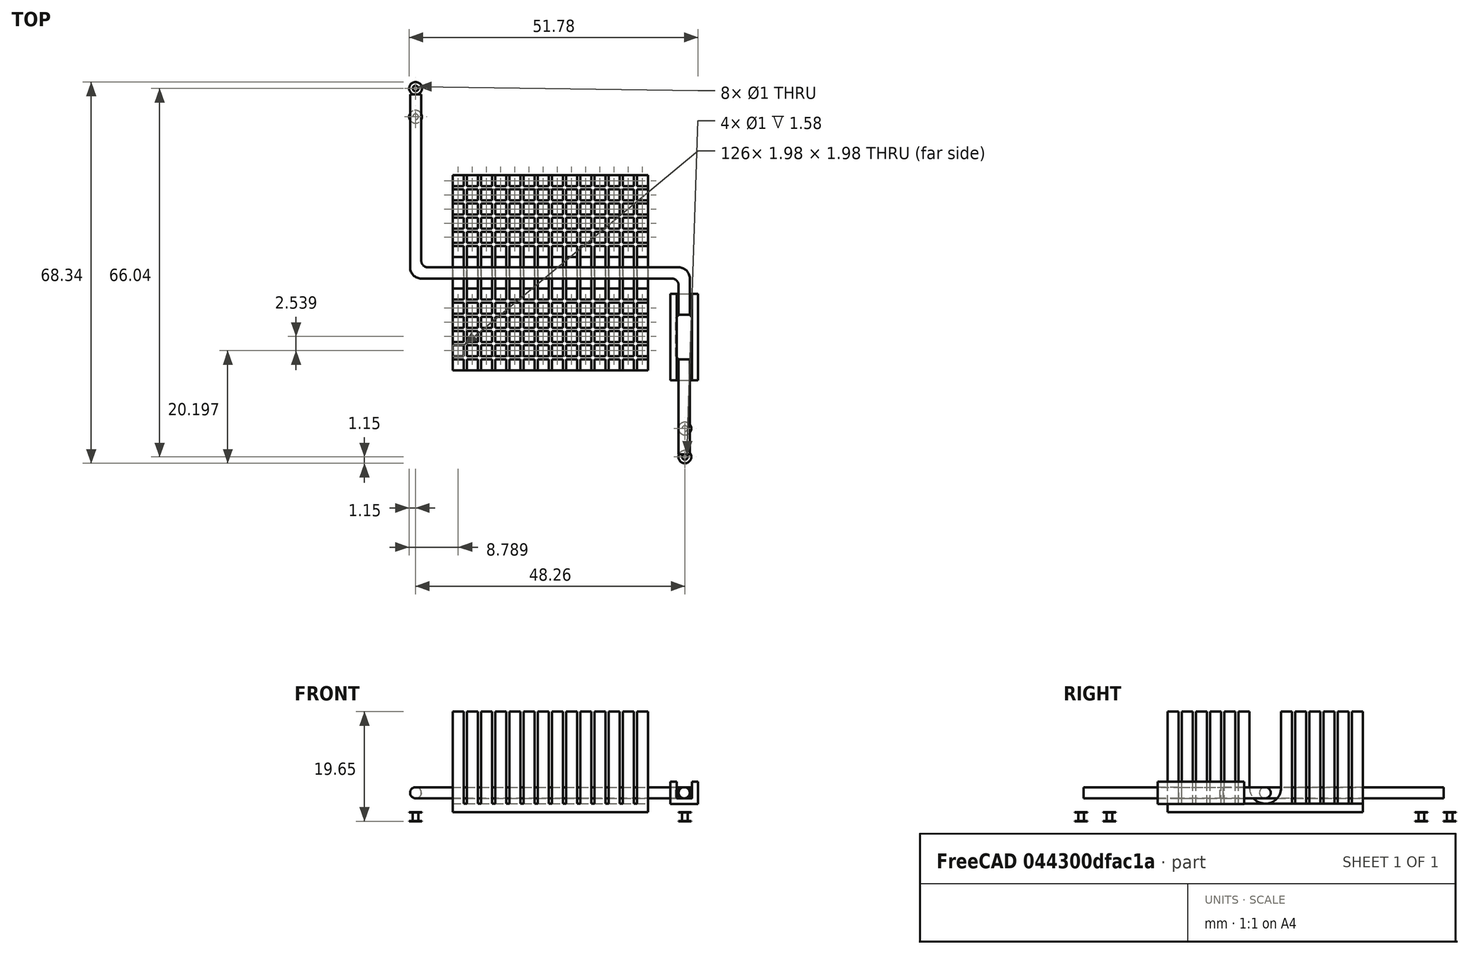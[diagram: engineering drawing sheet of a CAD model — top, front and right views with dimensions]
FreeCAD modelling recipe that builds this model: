
FCSTD DOCUMENT  (FreeCAD 0.20R29177 (Git))
Label: Aavid-heatsink2
License: All rights reserved
LicenseURL: http://en.wikipedia.org/wiki/All_rights_reserved
objects: PartDesign::AdditiveBox×7, PartDesign::Fillet×4, PartDesign::Body×4, Part::FeaturePython×3, Part::Feature×2, Sketcher::SketchObject×2, PartDesign::Chamfer×2, App::DocumentObjectGroup×1, PartDesign::SubtractiveBox×1, Part::Part2DObjectPython×1, PartDesign::Pad×1, App::Part×1
note: 41 computed .brp shape members not serialized (recipe doc carries the construction recipe); baked Part::Feature solids carry a one-line shape summary decoded from their .brp

FEATURE [Part::FeaturePython] FFab_lines  label="FFab"  # a2plus imported part (geometry in sourceFile) (typed FeaturePython)
  fixedPosition = true
FEATURE [Part::FeaturePython] THPs  label="PTHs"  # a2plus imported part (geometry in sourceFile) (typed FeaturePython)
  fixedPosition = true
FEATURE [Part::Feature] Shape001003  label="TopPads"
  shape: bbox 50.56 x 68.34 x 0.01 mm, 16 faces, 4 solids (baked)
FEATURE [Part::Feature] Shape001004  label="BotPads"
  shape: bbox 50.56 x 68.34 x 0.01 mm, 16 faces, 4 solids (baked)
FEATURE [App::DocumentObjectGroup] Heatsink_35x35mm_SpringFixation_fp
  Group = -> [FFab_lines,Shape001003,Shape001004,THPs]
FEATURE [Sketcher::SketchObject] Sketch  label="Pads_Poly"
  FullyConstrained = false
  MapMode = 5
  Support = -> [XY_Plane]
  sketch-geometry (56):
    g0: LineSegment StartX=-17.5 StartY=-17.45 StartZ=0 EndX=-17.5 EndY=17.55 EndZ=0
    g1: LineSegment StartX=-17.5 StartY=17.55 StartZ=0 EndX=-17.5 EndY=-17.55 EndZ=0
    g2: LineSegment StartX=-17.5 StartY=17.55 StartZ=0 EndX=17.55 EndY=17.5 EndZ=0
    g3: LineSegment StartX=17.55 StartY=17.5 StartZ=0 EndX=-17.5 EndY=17.45 EndZ=0
    g4: LineSegment StartX=17.55 StartY=17.5 StartZ=0 EndX=17.55 EndY=-17.5 EndZ=0
    g5: LineSegment StartX=17.5 StartY=-17.55 StartZ=0 EndX=17.45 EndY=17.5 EndZ=0
    g6: LineSegment StartX=17.5 StartY=-17.55 StartZ=0 EndX=-17.5 EndY=-17.55 EndZ=0
    g7: LineSegment StartX=-17.5 StartY=-17.45 StartZ=0 EndX=17.55 EndY=-17.5 EndZ=0
    g8: LineSegment StartX=-26.72 StartY=25.4 StartZ=0 EndX=-26.67 EndY=35.61 EndZ=0
    g9: LineSegment StartX=-26.67 StartY=35.61 StartZ=0 EndX=-26.62 EndY=25.4 EndZ=0
    g10: LineSegment StartX=-21.54 StartY=35.56 StartZ=0 EndX=-21.54 EndY=25.4 EndZ=0
    g11: LineSegment StartX=-21.64 StartY=25.4 StartZ=0 EndX=-21.64 EndY=35.56 EndZ=0
    g12: LineSegment StartX=-21.54 StartY=25.4 StartZ=0 EndX=-26.72 EndY=25.4 EndZ=0
    g13: LineSegment StartX=-26.72 StartY=25.4 StartZ=0 EndX=-21.54 EndY=25.4 EndZ=0
    g14: LineSegment StartX=-22.81 StartY=25.4 StartZ=0 EndX=-22.8271 EndY=2.54 EndZ=0
    g15: ArcOfCircle CenterX=-21.59 CenterY=2.55711 CenterZ=0 NormalX=0 NormalY=0 NormalZ=1 AngleXU=-1.5708 Radius=1.23726 StartAngle=4.72622 EndAngle=6.28319
    g16: LineSegment StartX=-21.59 StartY=1.31985 StartZ=0 EndX=-17.5 EndY=1.32 EndZ=0
    g17: LineSegment StartX=-17.5 StartY=1.22 StartZ=0 EndX=-21.59 EndY=1.29434 EndZ=0
    g18: ArcOfCircle CenterX=-21.5814 CenterY=2.54 CenterZ=0 NormalX=0 NormalY=0 NormalZ=1 AngleXU=-1.5708 Radius=1.24569 StartAngle=4.71239 EndAngle=6.27632
    g19: LineSegment StartX=-22.91 StartY=2.54 StartZ=0 EndX=-22.91 EndY=25.4 EndZ=0
    g20: LineSegment StartX=-25.35 StartY=1.27 StartZ=0 EndX=-25.45 EndY=25.4 EndZ=0
    g21: LineSegment StartX=-25.35 StartY=25.4 StartZ=0 EndX=-25.35 EndY=1.27 EndZ=0
    g22: ArcOfCircle CenterX=-22.86 CenterY=1.26185 CenterZ=0 NormalX=0 NormalY=0 NormalZ=1 AngleXU=-1.5708 Radius=2.49001 StartAngle=4.70911 EndAngle=6.28319
    g23: LineSegment StartX=-22.86 StartY=-1.22817 StartZ=0 EndX=-17.5 EndY=-1.22 EndZ=0
    g24: LineSegment StartX=-17.5 StartY=-1.32 StartZ=0 EndX=-22.86 EndY=-1.32 EndZ=0
    g25: ArcOfCircle CenterX=-22.86 CenterY=1.36352 CenterZ=0 NormalX=0 NormalY=0 NormalZ=1 AngleXU=-1.5708 Radius=2.59169 StartAngle=4.74848 EndAngle=6.28319
    g26: LineSegment StartX=-21.54 StartY=35.56 StartZ=0 EndX=-26.67 EndY=35.61 EndZ=0
    g27: LineSegment StartX=-26.67 StartY=35.61 StartZ=0 EndX=-21.54 EndY=35.56 EndZ=0
    g28: LineSegment StartX=21.59 StartY=-35.51 StartZ=0 EndX=21.59 EndY=-25.25 EndZ=0
    g29: LineSegment StartX=21.59 StartY=-25.25 StartZ=0 EndX=21.59 EndY=-35.51 EndZ=0
    g30: LineSegment StartX=26.67 StartY=-25.25 StartZ=0 EndX=26.72 EndY=-35.46 EndZ=0
    g31: LineSegment StartX=26.62 StartY=-35.46 StartZ=0 EndX=26.67 EndY=-25.25 EndZ=0
    g32: LineSegment StartX=21.59 StartY=-25.25 StartZ=0 EndX=26.67 EndY=-25.25 EndZ=0
    g33: LineSegment StartX=26.67 StartY=-25.35 StartZ=0 EndX=21.59 EndY=-25.35 EndZ=0
    g34: LineSegment StartX=25.35 StartY=-25.3 StartZ=0 EndX=25.35 EndY=-1.17 EndZ=0
    g35: ArcOfCircle CenterX=22.797 CenterY=-1.16077 CenterZ=0 NormalX=0 NormalY=0 NormalZ=1 AngleXU=1.5708 Radius=2.57229 StartAngle=4.7088 EndAngle=6.25869
    g36: LineSegment StartX=22.86 StartY=1.32 StartZ=0 EndX=17.5 EndY=1.32 EndZ=0
    g37: LineSegment StartX=17.5 StartY=1.42 StartZ=0 EndX=22.86 EndY=1.41075 EndZ=0
    g38: ArcOfCircle CenterX=22.86 CenterY=-1.17 CenterZ=0 NormalX=0 NormalY=0 NormalZ=1 AngleXU=1.5708 Radius=2.58075 StartAngle=4.71239 EndAngle=6.28319
    g39: LineSegment StartX=25.4407 StartY=-1.17 StartZ=0 EndX=25.45 EndY=-25.3 EndZ=0
    g40: LineSegment StartX=21.59 StartY=-35.51 StartZ=0 EndX=26.72 EndY=-35.46 EndZ=0
    g41: LineSegment StartX=26.72 StartY=-35.46 StartZ=0 EndX=21.59 EndY=-35.51 EndZ=0
    g42: LineSegment StartX=22.81 StartY=-2.44 StartZ=0 EndX=22.91 EndY=-25.3 EndZ=0
    g43: LineSegment StartX=22.81 StartY=-25.3 StartZ=0 EndX=22.81 EndY=-2.44 EndZ=0
    g44: ArcOfCircle CenterX=21.59 CenterY=-2.35008 CenterZ=0 NormalX=0 NormalY=0 NormalZ=1 AngleXU=1.5708 Radius=1.22331 StartAngle=4.63882 EndAngle=6.28319
    g45: LineSegment StartX=21.59 StartY=-1.12677 StartZ=0 EndX=17.5 EndY=-1.22 EndZ=0
    g46: LineSegment StartX=17.5 StartY=-1.12 StartZ=0 EndX=21.59 EndY=-1.12677 EndZ=0
    g47: ArcOfCircle CenterX=21.59 CenterY=-2.44679 CenterZ=0 NormalX=0 NormalY=0 NormalZ=1 AngleXU=1.5708 Radius=1.32002 StartAngle=4.71753 EndAngle=6.28319
    g48: LineSegment StartX=21.59 StartY=-18.525 StartZ=0 EndX=21.59 EndY=-3.125 EndZ=0
    g49: LineSegment StartX=21.59 StartY=-3.125 StartZ=0 EndX=21.59 EndY=-18.525 EndZ=0
    g50: LineSegment StartX=21.59 StartY=-18.525 StartZ=0 EndX=26.67 EndY=-18.525 EndZ=0
    g51: LineSegment StartX=26.67 StartY=-18.625 StartZ=0 EndX=21.59 EndY=-18.625 EndZ=0
    g52: LineSegment StartX=26.67 StartY=-18.525 StartZ=0 EndX=26.62 EndY=-3.075 EndZ=0
    g53: LineSegment StartX=26.72 StartY=-3.075 StartZ=0 EndX=26.67 EndY=-18.525 EndZ=0
    g54: LineSegment StartX=21.59 StartY=-3.125 StartZ=0 EndX=26.72 EndY=-3.075 EndZ=0
    g55: LineSegment StartX=26.72 StartY=-3.075 StartZ=0 EndX=21.59 EndY=-3.125 EndZ=0
  constraints (50):
    c: Coincident(g8,g12)
    c: Coincident(g8,g13)
    c: Coincident(g27,g8)
    c: Coincident(g27,g9)
    c: Coincident(g27,g26)
    c: Coincident(g22,g20)
    c: Coincident(g23,g25)
    c: Coincident(g23,g22)
    c: Coincident(g14,g15)
    c: Coincident(g14,g18)
    c: Coincident(g18,g17)
    c: Coincident(g15,g16)
    c: Coincident(g10,g12)
    c: Coincident(g10,g13)
    c: Coincident(g10,g26)
    c: Coincident(g10,g27)
    c: Coincident(g6,g1)
    c: Coincident(g7,g0)
    c: Coincident(g2,g0)
    c: Coincident(g2,g1)
    c: Coincident(g6,g5)
    c: Coincident(g4,g7)
    c: Coincident(g4,g3)
    c: Coincident(g4,g2)
    c: Coincident(g41,g28)
    c: Coincident(g41,g40)
    c: Coincident(g41,g29)
    c: Coincident(g32,g28)
    c: Coincident(g32,g29)
    c: Coincident(g50,g48)
    c: Coincident(g50,g49)
    c: Coincident(g55,g54)
    c: Coincident(g55,g48)
    c: Coincident(g55,g49)
    c: Coincident(g47,g45)
    c: Coincident(g47,g44)
    c: Coincident(g47,g46)
    c: Coincident(g44,g43)
    c: Coincident(g44,g42)
    c: Coincident(g37,g35)
    c: Coincident(g37,g38)
    c: Coincident(g39,g38)
    c: Coincident(g30,g40)
    c: Coincident(g30,g41)
    c: Coincident(g32,g31)
    c: Coincident(g32,g30)
    c: Coincident(g50,g52)
    c: Coincident(g50,g53)
    c: Coincident(g53,g54)
    c: Coincident(g53,g55)
FEATURE [PartDesign::AdditiveBox] Box  label="metal"
  AttacherType = Attacher::AttachEngine3D
  AttachmentOffset = pos=(-17.5,-17.5,0) rot=(0,0,1;0rad)
  Height = 1.5
  Length = 35
  MapMode = 5
  Placement = pos=(-17.5,-17.5,0) rot=(0,0,1;0rad)
  Support = -> [XY_Plane]
  Width = 35
FEATURE [PartDesign::AdditiveBox] Box010  label="base-lower-arm"
  AttacherType = Attacher::AttachEngine3D
  AttachmentOffset = pos=(23,-32,2.5) rot=(0,0,1;0rad)
  Height = 2
  Length = 2
  MapMode = 5
  Placement = pos=(23,-32,2.5) rot=(0,0,1;0rad)
  Support = -> [XY_Plane001]
  Width = 33.5
FEATURE [PartDesign::AdditiveBox] Box011  label="mid-arm"
  AttacherType = Attacher::AttachEngine3D
  AttachmentOffset = pos=(-23.1,-0.5,2.5) rot=(0,0,1;0rad)
  BaseFeature = -> Box010
  Height = 2
  Length = 46.1
  MapMode = 5
  Placement = pos=(-23.1,-0.5,2.5) rot=(0,0,1;0rad)
  Support = -> [XY_Plane001]
  Width = 2
FEATURE [PartDesign::AdditiveBox] Box012
  AttacherType = Attacher::AttachEngine3D
  AttachmentOffset = pos=(-25.1,-0.5,2.5) rot=(0,0,1;0rad)
  BaseFeature = -> Box011
  Height = 2
  Length = 2
  MapMode = 5
  Placement = pos=(-25.1,-0.5,2.5) rot=(0,0,1;0rad)
  Support = -> [XY_Plane001]
  Width = 33
FEATURE [PartDesign::Fillet] Fillet  label="outer-bend"
  Base = -> Box012 [Edge25,Edge19]
  BaseFeature = -> Box012
  Placement = pos=(-25.1,-0.5,2.5) rot=(0,0,1;0rad)
  Radius = 1.99
  SupportTransform = false
  UseAllEdges = false
FEATURE [PartDesign::Fillet] Fillet001  label="inner-bend"
  Base = -> Fillet [Edge17,Edge23]
  BaseFeature = -> Fillet
  Placement = pos=(-25.1,-0.5,2.5) rot=(0,0,1;0rad)
  Radius = 1.2
  SupportTransform = false
  UseAllEdges = false
FEATURE [PartDesign::Fillet] Fillet002  label="outer-smooth"
  Base = -> Fillet001 [Edge7,Edge5,Edge11,Edge12,Edge33,Edge20,Edge24,Edge29,Edge38,Edge25,Edge10,Edge50,Edge47,Edge43,Edge31,Edge1,Edge15,Edge16,Edge37,Edge35,Edge36]
  BaseFeature = -> Fillet001
  Placement = pos=(-25.1,-0.5,2.5) rot=(0,0,1;0rad)
  Radius = 0.99
  SupportTransform = false
  UseAllEdges = false
FEATURE [PartDesign::AdditiveBox] Box013
  AttacherType = Attacher::AttachEngine3D
  AttachmentOffset = pos=(22.5,-15,2.5) rot=(0,0,1;0rad)
  BaseFeature = -> Fillet002
  Height = 2
  Length = 3
  MapMode = 5
  Placement = pos=(22.5,-15,2.5) rot=(0,0,1;0rad)
  Support = -> [XY_Plane001]
  Width = 8
FEATURE [PartDesign::AdditiveBox] Box014
  AttacherType = Attacher::AttachEngine3D
  AttachmentOffset = pos=(21.5,-18.6,1.5) rot=(0,0,1;0rad)
  Height = 4
  Length = 5
  MapMode = 5
  Placement = pos=(21.5,-18.6,1.5) rot=(0,0,1;0rad)
  Support = -> [XY_Plane002]
  Width = 15.5
FEATURE [PartDesign::SubtractiveBox] Box015
  AttacherType = Attacher::AttachEngine3D
  AttachmentOffset = pos=(22.65,-19,2.5) rot=(0,0,1;0rad)
  BaseFeature = -> Box014
  Height = 3
  Length = 2.75
  MapMode = 5
  Placement = pos=(22.65,-19,2.5) rot=(0,0,1;0rad)
  Support = -> [XY_Plane002]
  Width = 16
FEATURE [PartDesign::Body] Body002  label="plastic-clamp"
  Group = -> [Box014,Box015]
  Origin = -> Origin002
  Placement = pos=(0,-0.7,0) rot=(0,0,1;0rad)
  Tip = -> Box015
FEATURE [PartDesign::AdditiveBox] Box016
  AttacherType = Attacher::AttachEngine3D
  AttachmentOffset = pos=(-15,-15,0) rot=(0,0,1;0rad)
  Height = 0.05
  Length = 30
  MapMode = 5
  Placement = pos=(-15,-15,0) rot=(0,0,1;0rad)
  Support = -> [XY_Plane004]
  Width = 30
FEATURE [PartDesign::Body] Body003  label="metal-film"
  Group = -> [Box016]
  Origin = -> Origin004
  Tip = -> Box016
FEATURE [Part::Part2DObjectPython] Shape2DView  # Draft 2D object (typed FeaturePython)
  AutoUpdate = true
  Clip = false
  FuseArch = false
  HiddenLines = false
  InPlace = true
  OnlySolids = false
  Projection = (0,0,1)
  ProjectionMode = 0
  SegmentLength = 0.05
  Tessellation = false
  VisibleOnly = false
FEATURE [Part::FeaturePython] Array  # Draft array (typed FeaturePython)
  AlwaysSyncPlacement = false
  Angle = 360
  ArrayType = 0
  Axis = (0,0,1)
  Base = -> Shape2DView
  Center = (0,0,0)
  Count = 196
  ExpandArray = false
  Fuse = false
  IntervalAxis = (0,0,0)
  IntervalX = (2.5387,0,0)
  IntervalY = (0,2.5387,0)
  IntervalZ = (0,0,100)
  NumberCircles = 3
  NumberPolar = 5
  NumberX = 14
  NumberY = 14
  NumberZ = 1
  Placement = pos=(0,-33.0245,0) rot=(0,0,1;0rad)
  PlacementList = 196 placements: [(0,0,0),(0,2.5387,0),(0,5.0774,0),(0,7.6161,0),(0,10.1548,0),(0,12.6935,0),(0,15.2322,0),(0,17.7709,0),(0,20.3096,0),(0,22.8483,0),(0,25.387,0),(0,27.9257,0),(0,30.4644,0),(0,33.0031,0),(2.5387,0,0),(2.5387,2.5387,0),(2.5387,5.0774,0),(2.5387,7.6161,0),(2.5387,10.1548,0),(2.5387,12.6935,0),(2.5387,15.2322,0),(2.5387,17.7709,0),(2.5387,20.3096,0),(2.5387,22.8483,0),(2.5387,25.387,0),+171 more]
  RadialDistance = 50
  ScaleList = (196) [(1,1,1),(1,1,1),(1,1,1),(1,1,1),(1,1,1),(1,1,1),(1,1,1),(1,1,1),(1,1,1),(1,1,1),(1,1,1),(1,1,1),(1,1,1),(1,1,1),(1,1,1),(1,1,1),(1,1,1),(1,1,1),+178 more]
  Symmetry = 1
  TangentialDistance = 25
FEATURE [Sketcher::SketchObject] Sketch001  label="fin-sketch"
  FullyConstrained = false
  sketch-geometry (672):
    g0: LineSegment StartX=-17.5 StartY=-17.5 StartZ=0 EndX=-17.5 EndY=-15.5245 EndZ=0
    g1: LineSegment StartX=-15.5245 StartY=-17.5 StartZ=0 EndX=-15.5245 EndY=-15.5245 EndZ=0
    g2: LineSegment StartX=-17.5 StartY=-17.5 StartZ=0 EndX=-15.5245 EndY=-17.5 EndZ=0
    g3: LineSegment StartX=-17.5 StartY=-15.5245 StartZ=0 EndX=-15.5245 EndY=-15.5245 EndZ=0
    g4: LineSegment StartX=-17.5 StartY=-14.9613 StartZ=0 EndX=-17.5 EndY=-12.9858 EndZ=0
    g5: LineSegment StartX=-15.5245 StartY=-14.9613 StartZ=0 EndX=-15.5245 EndY=-12.9858 EndZ=0
    g6: LineSegment StartX=-17.5 StartY=-14.9613 StartZ=0 EndX=-15.5245 EndY=-14.9613 EndZ=0
    g7: LineSegment StartX=-17.5 StartY=-12.9858 StartZ=0 EndX=-15.5245 EndY=-12.9858 EndZ=0
    g8: LineSegment StartX=-17.5 StartY=-12.4226 StartZ=0 EndX=-17.5 EndY=-10.4471 EndZ=0
    g9: LineSegment StartX=-15.5245 StartY=-12.4226 StartZ=0 EndX=-15.5245 EndY=-10.4471 EndZ=0
    g10: LineSegment StartX=-17.5 StartY=-12.4226 StartZ=0 EndX=-15.5245 EndY=-12.4226 EndZ=0
    g11: LineSegment StartX=-17.5 StartY=-10.4471 StartZ=0 EndX=-15.5245 EndY=-10.4471 EndZ=0
    g12: LineSegment StartX=-17.5 StartY=-9.88385 StartZ=0 EndX=-17.5 EndY=-7.90835 EndZ=0
    g13: LineSegment StartX=-15.5245 StartY=-9.88385 StartZ=0 EndX=-15.5245 EndY=-7.90835 EndZ=0
    g14: LineSegment StartX=-17.5 StartY=-9.88385 StartZ=0 EndX=-15.5245 EndY=-9.88385 EndZ=0
    g15: LineSegment StartX=-17.5 StartY=-7.90835 StartZ=0 EndX=-15.5245 EndY=-7.90835 EndZ=0
    g16: LineSegment StartX=-17.5 StartY=-7.34515 StartZ=0 EndX=-17.5 EndY=-5.36965 EndZ=0
    g17: LineSegment StartX=-15.5245 StartY=-7.34515 StartZ=0 EndX=-15.5245 EndY=-5.36965 EndZ=0
    g18: LineSegment StartX=-17.5 StartY=-7.34515 StartZ=0 EndX=-15.5245 EndY=-7.34515 EndZ=0
    g19: LineSegment StartX=-17.5 StartY=-5.36965 StartZ=0 EndX=-15.5245 EndY=-5.36965 EndZ=0
    g20: LineSegment StartX=-17.5 StartY=-4.80645 StartZ=0 EndX=-17.5 EndY=-2.83095 EndZ=0
    g21: LineSegment StartX=-15.5245 StartY=-4.80645 StartZ=0 EndX=-15.5245 EndY=-2.83095 EndZ=0
    g22: LineSegment StartX=-17.5 StartY=-4.80645 StartZ=0 EndX=-15.5245 EndY=-4.80645 EndZ=0
    g23: LineSegment StartX=-17.5 StartY=-2.83095 StartZ=0 EndX=-15.5245 EndY=-2.83095 EndZ=0
    g24: LineSegment StartX=-17.5 StartY=-2.26775 StartZ=0 EndX=-17.5 EndY=-0.292254 EndZ=0
    g25: LineSegment StartX=-15.5245 StartY=-2.26775 StartZ=0 EndX=-15.5245 EndY=-0.292254 EndZ=0
    g26: LineSegment StartX=-17.5 StartY=-2.26775 StartZ=0 EndX=-15.5245 EndY=-2.26775 EndZ=0
    g27: LineSegment StartX=-17.5 StartY=-0.292254 StartZ=0 EndX=-15.5245 EndY=-0.292254 EndZ=0
    g28: LineSegment StartX=-17.5 StartY=0.270946 StartZ=0 EndX=-17.5 EndY=2.24645 EndZ=0
    g29: LineSegment StartX=-15.5245 StartY=0.270946 StartZ=0 EndX=-15.5245 EndY=2.24645 EndZ=0
    g30: LineSegment StartX=-17.5 StartY=0.270946 StartZ=0 EndX=-15.5245 EndY=0.270946 EndZ=0
    g31: LineSegment StartX=-17.5 StartY=2.24645 StartZ=0 EndX=-15.5245 EndY=2.24645 EndZ=0
    g32: LineSegment StartX=-17.5 StartY=2.80965 StartZ=0 EndX=-17.5 EndY=4.78515 EndZ=0
    g33: LineSegment StartX=-15.5245 StartY=2.80965 StartZ=0 EndX=-15.5245 EndY=4.78515 EndZ=0
    g34: LineSegment StartX=-17.5 StartY=2.80965 StartZ=0 EndX=-15.5245 EndY=2.80965 EndZ=0
    g35: LineSegment StartX=-17.5 StartY=4.78515 StartZ=0 EndX=-15.5245 EndY=4.78515 EndZ=0
    g36: LineSegment StartX=-17.5 StartY=5.34835 StartZ=0 EndX=-17.5 EndY=7.32385 EndZ=0
    g37: LineSegment StartX=-15.5245 StartY=5.34835 StartZ=0 EndX=-15.5245 EndY=7.32385 EndZ=0
    g38: LineSegment StartX=-17.5 StartY=5.34835 StartZ=0 EndX=-15.5245 EndY=5.34835 EndZ=0
    g39: LineSegment StartX=-17.5 StartY=7.32385 StartZ=0 EndX=-15.5245 EndY=7.32385 EndZ=0
    g40: LineSegment StartX=-17.5 StartY=7.88705 StartZ=0 EndX=-17.5 EndY=9.86255 EndZ=0
    g41: LineSegment StartX=-15.5245 StartY=7.88705 StartZ=0 EndX=-15.5245 EndY=9.86255 EndZ=0
    g42: LineSegment StartX=-17.5 StartY=7.88705 StartZ=0 EndX=-15.5245 EndY=7.88705 EndZ=0
    g43: LineSegment StartX=-17.5 StartY=9.86255 StartZ=0 EndX=-15.5245 EndY=9.86255 EndZ=0
    g44: LineSegment StartX=-17.5 StartY=10.4257 StartZ=0 EndX=-17.5 EndY=12.4012 EndZ=0
    g45: LineSegment StartX=-15.5245 StartY=10.4257 StartZ=0 EndX=-15.5245 EndY=12.4012 EndZ=0
    g46: LineSegment StartX=-17.5 StartY=10.4257 StartZ=0 EndX=-15.5245 EndY=10.4257 EndZ=0
    g47: LineSegment StartX=-17.5 StartY=12.4012 StartZ=0 EndX=-15.5245 EndY=12.4012 EndZ=0
    g48: LineSegment StartX=-17.5 StartY=12.9644 StartZ=0 EndX=-17.5 EndY=14.9399 EndZ=0
    g49: LineSegment StartX=-15.5245 StartY=12.9644 StartZ=0 EndX=-15.5245 EndY=14.9399 EndZ=0
    g50: LineSegment StartX=-17.5 StartY=12.9644 StartZ=0 EndX=-15.5245 EndY=12.9644 EndZ=0
    g51: LineSegment StartX=-17.5 StartY=14.9399 StartZ=0 EndX=-15.5245 EndY=14.9399 EndZ=0
    g52: LineSegment StartX=-17.5 StartY=15.5031 StartZ=0 EndX=-17.5 EndY=17.4786 EndZ=0
    g53: LineSegment StartX=-15.5245 StartY=15.5031 StartZ=0 EndX=-15.5245 EndY=17.4786 EndZ=0
    g54: LineSegment StartX=-17.5 StartY=15.5031 StartZ=0 EndX=-15.5245 EndY=15.5031 EndZ=0
    g55: LineSegment StartX=-17.5 StartY=17.4786 StartZ=0 EndX=-15.5245 EndY=17.4786 EndZ=0
    g56: LineSegment StartX=-14.9613 StartY=-17.5 StartZ=0 EndX=-14.9613 EndY=-15.5245 EndZ=0
    g57: LineSegment StartX=-12.9858 StartY=-17.5 StartZ=0 EndX=-12.9858 EndY=-15.5245 EndZ=0
    g58: LineSegment StartX=-14.9613 StartY=-17.5 StartZ=0 EndX=-12.9858 EndY=-17.5 EndZ=0
    g59: LineSegment StartX=-14.9613 StartY=-15.5245 StartZ=0 EndX=-12.9858 EndY=-15.5245 EndZ=0
    g60: LineSegment StartX=-14.9613 StartY=-14.9613 StartZ=0 EndX=-14.9613 EndY=-12.9858 EndZ=0
    g61: LineSegment StartX=-12.9858 StartY=-14.9613 StartZ=0 EndX=-12.9858 EndY=-12.9858 EndZ=0
    g62: LineSegment StartX=-14.9613 StartY=-14.9613 StartZ=0 EndX=-12.9858 EndY=-14.9613 EndZ=0
    g63: LineSegment StartX=-14.9613 StartY=-12.9858 StartZ=0 EndX=-12.9858 EndY=-12.9858 EndZ=0
    g64: LineSegment StartX=-14.9613 StartY=-12.4226 StartZ=0 EndX=-14.9613 EndY=-10.4471 EndZ=0
    g65: LineSegment StartX=-12.9858 StartY=-12.4226 StartZ=0 EndX=-12.9858 EndY=-10.4471 EndZ=0
    g66: LineSegment StartX=-14.9613 StartY=-12.4226 StartZ=0 EndX=-12.9858 EndY=-12.4226 EndZ=0
    g67: LineSegment StartX=-14.9613 StartY=-10.4471 StartZ=0 EndX=-12.9858 EndY=-10.4471 EndZ=0
    g68: LineSegment StartX=-14.9613 StartY=-9.88385 StartZ=0 EndX=-14.9613 EndY=-7.90835 EndZ=0
    g69: LineSegment StartX=-12.9858 StartY=-9.88385 StartZ=0 EndX=-12.9858 EndY=-7.90835 EndZ=0
    g70: LineSegment StartX=-14.9613 StartY=-9.88385 StartZ=0 EndX=-12.9858 EndY=-9.88385 EndZ=0
    g71: LineSegment StartX=-14.9613 StartY=-7.90835 StartZ=0 EndX=-12.9858 EndY=-7.90835 EndZ=0
    g72: LineSegment StartX=-14.9613 StartY=-7.34515 StartZ=0 EndX=-14.9613 EndY=-5.36965 EndZ=0
    g73: LineSegment StartX=-12.9858 StartY=-7.34515 StartZ=0 EndX=-12.9858 EndY=-5.36965 EndZ=0
    g74: LineSegment StartX=-14.9613 StartY=-7.34515 StartZ=0 EndX=-12.9858 EndY=-7.34515 EndZ=0
    g75: LineSegment StartX=-14.9613 StartY=-5.36965 StartZ=0 EndX=-12.9858 EndY=-5.36965 EndZ=0
    g76: LineSegment StartX=-14.9613 StartY=-4.80645 StartZ=0 EndX=-14.9613 EndY=-2.83095 EndZ=0
    g77: LineSegment StartX=-12.9858 StartY=-4.80645 StartZ=0 EndX=-12.9858 EndY=-2.83095 EndZ=0
    g78: LineSegment StartX=-14.9613 StartY=-4.80645 StartZ=0 EndX=-12.9858 EndY=-4.80645 EndZ=0
    g79: LineSegment StartX=-14.9613 StartY=-2.83095 StartZ=0 EndX=-12.9858 EndY=-2.83095 EndZ=0
    g80: LineSegment StartX=-14.9613 StartY=-2.26775 StartZ=0 EndX=-14.9613 EndY=-0.292254 EndZ=0
    g81: LineSegment StartX=-12.9858 StartY=-2.26775 StartZ=0 EndX=-12.9858 EndY=-0.292254 EndZ=0
    g82: LineSegment StartX=-14.9613 StartY=-2.26775 StartZ=0 EndX=-12.9858 EndY=-2.26775 EndZ=0
    g83: LineSegment StartX=-14.9613 StartY=-0.292254 StartZ=0 EndX=-12.9858 EndY=-0.292254 EndZ=0
    g84: LineSegment StartX=-14.9613 StartY=0.270946 StartZ=0 EndX=-14.9613 EndY=2.24645 EndZ=0
    g85: LineSegment StartX=-12.9858 StartY=0.270946 StartZ=0 EndX=-12.9858 EndY=2.24645 EndZ=0
    g86: LineSegment StartX=-14.9613 StartY=0.270946 StartZ=0 EndX=-12.9858 EndY=0.270946 EndZ=0
    g87: LineSegment StartX=-14.9613 StartY=2.24645 StartZ=0 EndX=-12.9858 EndY=2.24645 EndZ=0
    g88: LineSegment StartX=-14.9613 StartY=2.80965 StartZ=0 EndX=-14.9613 EndY=4.78515 EndZ=0
    g89: LineSegment StartX=-12.9858 StartY=2.80965 StartZ=0 EndX=-12.9858 EndY=4.78515 EndZ=0
    g90: LineSegment StartX=-14.9613 StartY=2.80965 StartZ=0 EndX=-12.9858 EndY=2.80965 EndZ=0
    g91: LineSegment StartX=-14.9613 StartY=4.78515 StartZ=0 EndX=-12.9858 EndY=4.78515 EndZ=0
    g92: LineSegment StartX=-14.9613 StartY=5.34835 StartZ=0 EndX=-14.9613 EndY=7.32385 EndZ=0
    g93: LineSegment StartX=-12.9858 StartY=5.34835 StartZ=0 EndX=-12.9858 EndY=7.32385 EndZ=0
    g94: LineSegment StartX=-14.9613 StartY=5.34835 StartZ=0 EndX=-12.9858 EndY=5.34835 EndZ=0
    g95: LineSegment StartX=-14.9613 StartY=7.32385 StartZ=0 EndX=-12.9858 EndY=7.32385 EndZ=0
    g96: LineSegment StartX=-14.9613 StartY=7.88705 StartZ=0 EndX=-14.9613 EndY=9.86255 EndZ=0
    g97: LineSegment StartX=-12.9858 StartY=7.88705 StartZ=0 EndX=-12.9858 EndY=9.86255 EndZ=0
    g98: LineSegment StartX=-14.9613 StartY=7.88705 StartZ=0 EndX=-12.9858 EndY=7.88705 EndZ=0
    g99: LineSegment StartX=-14.9613 StartY=9.86255 StartZ=0 EndX=-12.9858 EndY=9.86255 EndZ=0
    g100: LineSegment StartX=-14.9613 StartY=10.4257 StartZ=0 EndX=-14.9613 EndY=12.4012 EndZ=0
    g101: LineSegment StartX=-12.9858 StartY=10.4257 StartZ=0 EndX=-12.9858 EndY=12.4012 EndZ=0
    g102: LineSegment StartX=-14.9613 StartY=10.4257 StartZ=0 EndX=-12.9858 EndY=10.4257 EndZ=0
    g103: LineSegment StartX=-14.9613 StartY=12.4012 StartZ=0 EndX=-12.9858 EndY=12.4012 EndZ=0
    g104: LineSegment StartX=-14.9613 StartY=12.9644 StartZ=0 EndX=-14.9613 EndY=14.9399 EndZ=0
    g105: LineSegment StartX=-12.9858 StartY=12.9644 StartZ=0 EndX=-12.9858 EndY=14.9399 EndZ=0
    g106: LineSegment StartX=-14.9613 StartY=12.9644 StartZ=0 EndX=-12.9858 EndY=12.9644 EndZ=0
    g107: LineSegment StartX=-14.9613 StartY=14.9399 StartZ=0 EndX=-12.9858 EndY=14.9399 EndZ=0
    g108: LineSegment StartX=-14.9613 StartY=15.5031 StartZ=0 EndX=-14.9613 EndY=17.4786 EndZ=0
    g109: LineSegment StartX=-12.9858 StartY=15.5031 StartZ=0 EndX=-12.9858 EndY=17.4786 EndZ=0
    g110: LineSegment StartX=-14.9613 StartY=15.5031 StartZ=0 EndX=-12.9858 EndY=15.5031 EndZ=0
    g111: LineSegment StartX=-14.9613 StartY=17.4786 StartZ=0 EndX=-12.9858 EndY=17.4786 EndZ=0
    g112: LineSegment StartX=-12.4226 StartY=-17.5 StartZ=0 EndX=-12.4226 EndY=-15.5245 EndZ=0
    g113: LineSegment StartX=-10.4471 StartY=-17.5 StartZ=0 EndX=-10.4471 EndY=-15.5245 EndZ=0
    g114: LineSegment StartX=-12.4226 StartY=-17.5 StartZ=0 EndX=-10.4471 EndY=-17.5 EndZ=0
    g115: LineSegment StartX=-12.4226 StartY=-15.5245 StartZ=0 EndX=-10.4471 EndY=-15.5245 EndZ=0
    g116: LineSegment StartX=-12.4226 StartY=-14.9613 StartZ=0 EndX=-12.4226 EndY=-12.9858 EndZ=0
    g117: LineSegment StartX=-10.4471 StartY=-14.9613 StartZ=0 EndX=-10.4471 EndY=-12.9858 EndZ=0
    g118: LineSegment StartX=-12.4226 StartY=-14.9613 StartZ=0 EndX=-10.4471 EndY=-14.9613 EndZ=0
    g119: LineSegment StartX=-12.4226 StartY=-12.9858 StartZ=0 EndX=-10.4471 EndY=-12.9858 EndZ=0
    g120: LineSegment StartX=-12.4226 StartY=-12.4226 StartZ=0 EndX=-12.4226 EndY=-10.4471 EndZ=0
    g121: LineSegment StartX=-10.4471 StartY=-12.4226 StartZ=0 EndX=-10.4471 EndY=-10.4471 EndZ=0
    g122: LineSegment StartX=-12.4226 StartY=-12.4226 StartZ=0 EndX=-10.4471 EndY=-12.4226 EndZ=0
    g123: LineSegment StartX=-12.4226 StartY=-10.4471 StartZ=0 EndX=-10.4471 EndY=-10.4471 EndZ=0
    g124: LineSegment StartX=-12.4226 StartY=-9.88385 StartZ=0 EndX=-12.4226 EndY=-7.90835 EndZ=0
    g125: LineSegment StartX=-10.4471 StartY=-9.88385 StartZ=0 EndX=-10.4471 EndY=-7.90835 EndZ=0
    g126: LineSegment StartX=-12.4226 StartY=-9.88385 StartZ=0 EndX=-10.4471 EndY=-9.88385 EndZ=0
    g127: LineSegment StartX=-12.4226 StartY=-7.90835 StartZ=0 EndX=-10.4471 EndY=-7.90835 EndZ=0
    g128: LineSegment StartX=-12.4226 StartY=-7.34515 StartZ=0 EndX=-12.4226 EndY=-5.36965 EndZ=0
    g129: LineSegment StartX=-10.4471 StartY=-7.34515 StartZ=0 EndX=-10.4471 EndY=-5.36965 EndZ=0
    g130: LineSegment StartX=-12.4226 StartY=-7.34515 StartZ=0 EndX=-10.4471 EndY=-7.34515 EndZ=0
    g131: LineSegment StartX=-12.4226 StartY=-5.36965 StartZ=0 EndX=-10.4471 EndY=-5.36965 EndZ=0
    g132: LineSegment StartX=-12.4226 StartY=-4.80645 StartZ=0 EndX=-12.4226 EndY=-2.83095 EndZ=0
    g133: LineSegment StartX=-10.4471 StartY=-4.80645 StartZ=0 EndX=-10.4471 EndY=-2.83095 EndZ=0
    g134: LineSegment StartX=-12.4226 StartY=-4.80645 StartZ=0 EndX=-10.4471 EndY=-4.80645 EndZ=0
    g135: LineSegment StartX=-12.4226 StartY=-2.83095 StartZ=0 EndX=-10.4471 EndY=-2.83095 EndZ=0
    g136: LineSegment StartX=-12.4226 StartY=-2.26775 StartZ=0 EndX=-12.4226 EndY=-0.292254 EndZ=0
    g137: LineSegment StartX=-10.4471 StartY=-2.26775 StartZ=0 EndX=-10.4471 EndY=-0.292254 EndZ=0
    g138: LineSegment StartX=-12.4226 StartY=-2.26775 StartZ=0 EndX=-10.4471 EndY=-2.26775 EndZ=0
    g139: LineSegment StartX=-12.4226 StartY=-0.292254 StartZ=0 EndX=-10.4471 EndY=-0.292254 EndZ=0
    g140: LineSegment StartX=-12.4226 StartY=0.270946 StartZ=0 EndX=-12.4226 EndY=2.24645 EndZ=0
    g141: LineSegment StartX=-10.4471 StartY=0.270946 StartZ=0 EndX=-10.4471 EndY=2.24645 EndZ=0
    g142: LineSegment StartX=-12.4226 StartY=0.270946 StartZ=0 EndX=-10.4471 EndY=0.270946 EndZ=0
    g143: LineSegment StartX=-12.4226 StartY=2.24645 StartZ=0 EndX=-10.4471 EndY=2.24645 EndZ=0
    g144: LineSegment StartX=-12.4226 StartY=2.80965 StartZ=0 EndX=-12.4226 EndY=4.78515 EndZ=0
    g145: LineSegment StartX=-10.4471 StartY=2.80965 StartZ=0 EndX=-10.4471 EndY=4.78515 EndZ=0
    g146: LineSegment StartX=-12.4226 StartY=2.80965 StartZ=0 EndX=-10.4471 EndY=2.80965 EndZ=0
    g147: LineSegment StartX=-12.4226 StartY=4.78515 StartZ=0 EndX=-10.4471 EndY=4.78515 EndZ=0
    g148: LineSegment StartX=-12.4226 StartY=5.34835 StartZ=0 EndX=-12.4226 EndY=7.32385 EndZ=0
    g149: LineSegment StartX=-10.4471 StartY=5.34835 StartZ=0 EndX=-10.4471 EndY=7.32385 EndZ=0
    g150: LineSegment StartX=-12.4226 StartY=5.34835 StartZ=0 EndX=-10.4471 EndY=5.34835 EndZ=0
    g151: LineSegment StartX=-12.4226 StartY=7.32385 StartZ=0 EndX=-10.4471 EndY=7.32385 EndZ=0
    g152: LineSegment StartX=-12.4226 StartY=7.88705 StartZ=0 EndX=-12.4226 EndY=9.86255 EndZ=0
    g153: LineSegment StartX=-10.4471 StartY=7.88705 StartZ=0 EndX=-10.4471 EndY=9.86255 EndZ=0
    g154: LineSegment StartX=-12.4226 StartY=7.88705 StartZ=0 EndX=-10.4471 EndY=7.88705 EndZ=0
    g155: LineSegment StartX=-12.4226 StartY=9.86255 StartZ=0 EndX=-10.4471 EndY=9.86255 EndZ=0
    g156: LineSegment StartX=-12.4226 StartY=10.4257 StartZ=0 EndX=-12.4226 EndY=12.4012 EndZ=0
    g157: LineSegment StartX=-10.4471 StartY=10.4257 StartZ=0 EndX=-10.4471 EndY=12.4012 EndZ=0
    g158: LineSegment StartX=-12.4226 StartY=10.4257 StartZ=0 EndX=-10.4471 EndY=10.4257 EndZ=0
    g159: LineSegment StartX=-12.4226 StartY=12.4012 StartZ=0 EndX=-10.4471 EndY=12.4012 EndZ=0
    g160: LineSegment StartX=-12.4226 StartY=12.9644 StartZ=0 EndX=-12.4226 EndY=14.9399 EndZ=0
    g161: LineSegment StartX=-10.4471 StartY=12.9644 StartZ=0 EndX=-10.4471 EndY=14.9399 EndZ=0
    g162: LineSegment StartX=-12.4226 StartY=12.9644 StartZ=0 EndX=-10.4471 EndY=12.9644 EndZ=0
    g163: LineSegment StartX=-12.4226 StartY=14.9399 StartZ=0 EndX=-10.4471 EndY=14.9399 EndZ=0
    g164: LineSegment StartX=-12.4226 StartY=15.5031 StartZ=0 EndX=-12.4226 EndY=17.4786 EndZ=0
    g165: LineSegment StartX=-10.4471 StartY=15.5031 StartZ=0 EndX=-10.4471 EndY=17.4786 EndZ=0
    g166: LineSegment StartX=-12.4226 StartY=15.5031 StartZ=0 EndX=-10.4471 EndY=15.5031 EndZ=0
    g167: LineSegment StartX=-12.4226 StartY=17.4786 StartZ=0 EndX=-10.4471 EndY=17.4786 EndZ=0
    g168: LineSegment StartX=-9.8839 StartY=-17.5 StartZ=0 EndX=-9.8839 EndY=-15.5245 EndZ=0
    g169: LineSegment StartX=-7.9084 StartY=-17.5 StartZ=0 EndX=-7.9084 EndY=-15.5245 EndZ=0
    g170: LineSegment StartX=-9.8839 StartY=-17.5 StartZ=0 EndX=-7.9084 EndY=-17.5 EndZ=0
    g171: LineSegment StartX=-9.8839 StartY=-15.5245 StartZ=0 EndX=-7.9084 EndY=-15.5245 EndZ=0
    g172: LineSegment StartX=-9.8839 StartY=-14.9613 StartZ=0 EndX=-9.8839 EndY=-12.9858 EndZ=0
    g173: LineSegment StartX=-7.9084 StartY=-14.9613 StartZ=0 EndX=-7.9084 EndY=-12.9858 EndZ=0
    g174: LineSegment StartX=-9.8839 StartY=-14.9613 StartZ=0 EndX=-7.9084 EndY=-14.9613 EndZ=0
    g175: LineSegment StartX=-9.8839 StartY=-12.9858 StartZ=0 EndX=-7.9084 EndY=-12.9858 EndZ=0
    g176: LineSegment StartX=-9.8839 StartY=-12.4226 StartZ=0 EndX=-9.8839 EndY=-10.4471 EndZ=0
    g177: LineSegment StartX=-7.9084 StartY=-12.4226 StartZ=0 EndX=-7.9084 EndY=-10.4471 EndZ=0
    g178: LineSegment StartX=-9.8839 StartY=-12.4226 StartZ=0 EndX=-7.9084 EndY=-12.4226 EndZ=0
    g179: LineSegment StartX=-9.8839 StartY=-10.4471 StartZ=0 EndX=-7.9084 EndY=-10.4471 EndZ=0
    g180: LineSegment StartX=-9.8839 StartY=-9.88385 StartZ=0 EndX=-9.8839 EndY=-7.90835 EndZ=0
    g181: LineSegment StartX=-7.9084 StartY=-9.88385 StartZ=0 EndX=-7.9084 EndY=-7.90835 EndZ=0
    g182: LineSegment StartX=-9.8839 StartY=-9.88385 StartZ=0 EndX=-7.9084 EndY=-9.88385 EndZ=0
    g183: LineSegment StartX=-9.8839 StartY=-7.90835 StartZ=0 EndX=-7.9084 EndY=-7.90835 EndZ=0
    g184: LineSegment StartX=-9.8839 StartY=-7.34515 StartZ=0 EndX=-9.8839 EndY=-5.36965 EndZ=0
    g185: LineSegment StartX=-7.9084 StartY=-7.34515 StartZ=0 EndX=-7.9084 EndY=-5.36965 EndZ=0
    g186: LineSegment StartX=-9.8839 StartY=-7.34515 StartZ=0 EndX=-7.9084 EndY=-7.34515 EndZ=0
    g187: LineSegment StartX=-9.8839 StartY=-5.36965 StartZ=0 EndX=-7.9084 EndY=-5.36965 EndZ=0
    g188: LineSegment StartX=-9.8839 StartY=-4.80645 StartZ=0 EndX=-9.8839 EndY=-2.83095 EndZ=0
    g189: LineSegment StartX=-7.9084 StartY=-4.80645 StartZ=0 EndX=-7.9084 EndY=-2.83095 EndZ=0
    g190: LineSegment StartX=-9.8839 StartY=-4.80645 StartZ=0 EndX=-7.9084 EndY=-4.80645 EndZ=0
    g191: LineSegment StartX=-9.8839 StartY=-2.83095 StartZ=0 EndX=-7.9084 EndY=-2.83095 EndZ=0
    g192: LineSegment StartX=-9.8839 StartY=-2.26775 StartZ=0 EndX=-9.8839 EndY=-0.292254 EndZ=0
    g193: LineSegment StartX=-7.9084 StartY=-2.26775 StartZ=0 EndX=-7.9084 EndY=-0.292254 EndZ=0
    g194: LineSegment StartX=-9.8839 StartY=-2.26775 StartZ=0 EndX=-7.9084 EndY=-2.26775 EndZ=0
    g195: LineSegment StartX=-9.8839 StartY=-0.292254 StartZ=0 EndX=-7.9084 EndY=-0.292254 EndZ=0
    g196: LineSegment StartX=-9.8839 StartY=0.270946 StartZ=0 EndX=-9.8839 EndY=2.24645 EndZ=0
    g197: LineSegment StartX=-7.9084 StartY=0.270946 StartZ=0 EndX=-7.9084 EndY=2.24645 EndZ=0
    g198: LineSegment StartX=-9.8839 StartY=0.270946 StartZ=0 EndX=-7.9084 EndY=0.270946 EndZ=0
    g199: LineSegment StartX=-9.8839 StartY=2.24645 StartZ=0 EndX=-7.9084 EndY=2.24645 EndZ=0
    g200: LineSegment StartX=-9.8839 StartY=2.80965 StartZ=0 EndX=-9.8839 EndY=4.78515 EndZ=0
    g201: LineSegment StartX=-7.9084 StartY=2.80965 StartZ=0 EndX=-7.9084 EndY=4.78515 EndZ=0
    g202: LineSegment StartX=-9.8839 StartY=2.80965 StartZ=0 EndX=-7.9084 EndY=2.80965 EndZ=0
    g203: LineSegment StartX=-9.8839 StartY=4.78515 StartZ=0 EndX=-7.9084 EndY=4.78515 EndZ=0
    g204: LineSegment StartX=-9.8839 StartY=5.34835 StartZ=0 EndX=-9.8839 EndY=7.32385 EndZ=0
    g205: LineSegment StartX=-7.9084 StartY=5.34835 StartZ=0 EndX=-7.9084 EndY=7.32385 EndZ=0
    g206: LineSegment StartX=-9.8839 StartY=5.34835 StartZ=0 EndX=-7.9084 EndY=5.34835 EndZ=0
    g207: LineSegment StartX=-9.8839 StartY=7.32385 StartZ=0 EndX=-7.9084 EndY=7.32385 EndZ=0
    g208: LineSegment StartX=-9.8839 StartY=7.88705 StartZ=0 EndX=-9.8839 EndY=9.86255 EndZ=0
    g209: LineSegment StartX=-7.9084 StartY=7.88705 StartZ=0 EndX=-7.9084 EndY=9.86255 EndZ=0
    g210: LineSegment StartX=-9.8839 StartY=7.88705 StartZ=0 EndX=-7.9084 EndY=7.88705 EndZ=0
    g211: LineSegment StartX=-9.8839 StartY=9.86255 StartZ=0 EndX=-7.9084 EndY=9.86255 EndZ=0
    g212: LineSegment StartX=-9.8839 StartY=10.4257 StartZ=0 EndX=-9.8839 EndY=12.4012 EndZ=0
    g213: LineSegment StartX=-7.9084 StartY=10.4257 StartZ=0 EndX=-7.9084 EndY=12.4012 EndZ=0
    g214: LineSegment StartX=-9.8839 StartY=10.4257 StartZ=0 EndX=-7.9084 EndY=10.4257 EndZ=0
    g215: LineSegment StartX=-9.8839 StartY=12.4012 StartZ=0 EndX=-7.9084 EndY=12.4012 EndZ=0
    g216: LineSegment StartX=-9.8839 StartY=12.9644 StartZ=0 EndX=-9.8839 EndY=14.9399 EndZ=0
    g217: LineSegment StartX=-7.9084 StartY=12.9644 StartZ=0 EndX=-7.9084 EndY=14.9399 EndZ=0
    g218: LineSegment StartX=-9.8839 StartY=12.9644 StartZ=0 EndX=-7.9084 EndY=12.9644 EndZ=0
    g219: LineSegment StartX=-9.8839 StartY=14.9399 StartZ=0 EndX=-7.9084 EndY=14.9399 EndZ=0
    g220: LineSegment StartX=-9.8839 StartY=15.5031 StartZ=0 EndX=-9.8839 EndY=17.4786 EndZ=0
    g221: LineSegment StartX=-7.9084 StartY=15.5031 StartZ=0 EndX=-7.9084 EndY=17.4786 EndZ=0
    g222: LineSegment StartX=-9.8839 StartY=15.5031 StartZ=0 EndX=-7.9084 EndY=15.5031 EndZ=0
    g223: LineSegment StartX=-9.8839 StartY=17.4786 StartZ=0 EndX=-7.9084 EndY=17.4786 EndZ=0
    g224: LineSegment StartX=-7.3452 StartY=-17.5 StartZ=0 EndX=-7.3452 EndY=-15.5245 EndZ=0
    g225: LineSegment StartX=-5.3697 StartY=-17.5 StartZ=0 EndX=-5.3697 EndY=-15.5245 EndZ=0
    g226: LineSegment StartX=-7.3452 StartY=-17.5 StartZ=0 EndX=-5.3697 EndY=-17.5 EndZ=0
    g227: LineSegment StartX=-7.3452 StartY=-15.5245 StartZ=0 EndX=-5.3697 EndY=-15.5245 EndZ=0
    g228: LineSegment StartX=-7.3452 StartY=-14.9613 StartZ=0 EndX=-7.3452 EndY=-12.9858 EndZ=0
    g229: LineSegment StartX=-5.3697 StartY=-14.9613 StartZ=0 EndX=-5.3697 EndY=-12.9858 EndZ=0
    g230: LineSegment StartX=-7.3452 StartY=-14.9613 StartZ=0 EndX=-5.3697 EndY=-14.9613 EndZ=0
    g231: LineSegment StartX=-7.3452 StartY=-12.9858 StartZ=0 EndX=-5.3697 EndY=-12.9858 EndZ=0
    g232: LineSegment StartX=-7.3452 StartY=-12.4226 StartZ=0 EndX=-7.3452 EndY=-10.4471 EndZ=0
    g233: LineSegment StartX=-5.3697 StartY=-12.4226 StartZ=0 EndX=-5.3697 EndY=-10.4471 EndZ=0
    g234: LineSegment StartX=-7.3452 StartY=-12.4226 StartZ=0 EndX=-5.3697 EndY=-12.4226 EndZ=0
    g235: LineSegment StartX=-7.3452 StartY=-10.4471 StartZ=0 EndX=-5.3697 EndY=-10.4471 EndZ=0
    g236: LineSegment StartX=-7.3452 StartY=-9.88385 StartZ=0 EndX=-7.3452 EndY=-7.90835 EndZ=0
    g237: LineSegment StartX=-5.3697 StartY=-9.88385 StartZ=0 EndX=-5.3697 EndY=-7.90835 EndZ=0
    g238: LineSegment StartX=-7.3452 StartY=-9.88385 StartZ=0 EndX=-5.3697 EndY=-9.88385 EndZ=0
    g239: LineSegment StartX=-7.3452 StartY=-7.90835 StartZ=0 EndX=-5.3697 EndY=-7.90835 EndZ=0
    g240: LineSegment StartX=-7.3452 StartY=-7.34515 StartZ=0 EndX=-7.3452 EndY=-5.36965 EndZ=0
    g241: LineSegment StartX=-5.3697 StartY=-7.34515 StartZ=0 EndX=-5.3697 EndY=-5.36965 EndZ=0
    g242: LineSegment StartX=-7.3452 StartY=-7.34515 StartZ=0 EndX=-5.3697 EndY=-7.34515 EndZ=0
    g243: LineSegment StartX=-7.3452 StartY=-5.36965 StartZ=0 EndX=-5.3697 EndY=-5.36965 EndZ=0
    g244: LineSegment StartX=-7.3452 StartY=-4.80645 StartZ=0 EndX=-7.3452 EndY=-2.83095 EndZ=0
    g245: LineSegment StartX=-5.3697 StartY=-4.80645 StartZ=0 EndX=-5.3697 EndY=-2.83095 EndZ=0
    g246: LineSegment StartX=-7.3452 StartY=-4.80645 StartZ=0 EndX=-5.3697 EndY=-4.80645 EndZ=0
    g247: LineSegment StartX=-7.3452 StartY=-2.83095 StartZ=0 EndX=-5.3697 EndY=-2.83095 EndZ=0
    g248: LineSegment StartX=-7.3452 StartY=-2.26775 StartZ=0 EndX=-7.3452 EndY=-0.292254 EndZ=0
    g249: LineSegment StartX=-5.3697 StartY=-2.26775 StartZ=0 EndX=-5.3697 EndY=-0.292254 EndZ=0
    g250: LineSegment StartX=-7.3452 StartY=-2.26775 StartZ=0 EndX=-5.3697 EndY=-2.26775 EndZ=0
    g251: LineSegment StartX=-7.3452 StartY=-0.292254 StartZ=0 EndX=-5.3697 EndY=-0.292254 EndZ=0
    g252: LineSegment StartX=-7.3452 StartY=0.270946 StartZ=0 EndX=-7.3452 EndY=2.24645 EndZ=0
    g253: LineSegment StartX=-5.3697 StartY=0.270946 StartZ=0 EndX=-5.3697 EndY=2.24645 EndZ=0
    g254: LineSegment StartX=-7.3452 StartY=0.270946 StartZ=0 EndX=-5.3697 EndY=0.270946 EndZ=0
    g255: LineSegment StartX=-7.3452 StartY=2.24645 StartZ=0 EndX=-5.3697 EndY=2.24645 EndZ=0
    g256: LineSegment StartX=-7.3452 StartY=2.80965 StartZ=0 EndX=-7.3452 EndY=4.78515 EndZ=0
    g257: LineSegment StartX=-5.3697 StartY=2.80965 StartZ=0 EndX=-5.3697 EndY=4.78515 EndZ=0
    g258: LineSegment StartX=-7.3452 StartY=2.80965 StartZ=0 EndX=-5.3697 EndY=2.80965 EndZ=0
    g259: LineSegment StartX=-7.3452 StartY=4.78515 StartZ=0 EndX=-5.3697 EndY=4.78515 EndZ=0
    g260: LineSegment StartX=-7.3452 StartY=5.34835 StartZ=0 EndX=-7.3452 EndY=7.32385 EndZ=0
    g261: LineSegment StartX=-5.3697 StartY=5.34835 StartZ=0 EndX=-5.3697 EndY=7.32385 EndZ=0
    g262: LineSegment StartX=-7.3452 StartY=5.34835 StartZ=0 EndX=-5.3697 EndY=5.34835 EndZ=0
    g263: LineSegment StartX=-7.3452 StartY=7.32385 StartZ=0 EndX=-5.3697 EndY=7.32385 EndZ=0
    g264: LineSegment StartX=-7.3452 StartY=7.88705 StartZ=0 EndX=-7.3452 EndY=9.86255 EndZ=0
    g265: LineSegment StartX=-5.3697 StartY=7.88705 StartZ=0 EndX=-5.3697 EndY=9.86255 EndZ=0
    g266: LineSegment StartX=-7.3452 StartY=7.88705 StartZ=0 EndX=-5.3697 EndY=7.88705 EndZ=0
    g267: LineSegment StartX=-7.3452 StartY=9.86255 StartZ=0 EndX=-5.3697 EndY=9.86255 EndZ=0
    g268: LineSegment StartX=-7.3452 StartY=10.4257 StartZ=0 EndX=-7.3452 EndY=12.4012 EndZ=0
    g269: LineSegment StartX=-5.3697 StartY=10.4257 StartZ=0 EndX=-5.3697 EndY=12.4012 EndZ=0
    g270: LineSegment StartX=-7.3452 StartY=10.4257 StartZ=0 EndX=-5.3697 EndY=10.4257 EndZ=0
    g271: LineSegment StartX=-7.3452 StartY=12.4012 StartZ=0 EndX=-5.3697 EndY=12.4012 EndZ=0
    g272: LineSegment StartX=-7.3452 StartY=12.9644 StartZ=0 EndX=-7.3452 EndY=14.9399 EndZ=0
    g273: LineSegment StartX=-5.3697 StartY=12.9644 StartZ=0 EndX=-5.3697 EndY=14.9399 EndZ=0
    g274: LineSegment StartX=-7.3452 StartY=12.9644 StartZ=0 EndX=-5.3697 EndY=12.9644 EndZ=0
    g275: LineSegment StartX=-7.3452 StartY=14.9399 StartZ=0 EndX=-5.3697 EndY=14.9399 EndZ=0
    g276: LineSegment StartX=-7.3452 StartY=15.5031 StartZ=0 EndX=-7.3452 EndY=17.4786 EndZ=0
    g277: LineSegment StartX=-5.3697 StartY=15.5031 StartZ=0 EndX=-5.3697 EndY=17.4786 EndZ=0
    g278: LineSegment StartX=-7.3452 StartY=15.5031 StartZ=0 EndX=-5.3697 EndY=15.5031 EndZ=0
    g279: LineSegment StartX=-7.3452 StartY=17.4786 StartZ=0 EndX=-5.3697 EndY=17.4786 EndZ=0
    g280: LineSegment StartX=-4.8065 StartY=-17.5 StartZ=0 EndX=-4.8065 EndY=-15.5245 EndZ=0
    g281: LineSegment StartX=-2.831 StartY=-17.5 StartZ=0 EndX=-2.831 EndY=-15.5245 EndZ=0
    g282: LineSegment StartX=-4.8065 StartY=-17.5 StartZ=0 EndX=-2.831 EndY=-17.5 EndZ=0
    g283: LineSegment StartX=-4.8065 StartY=-15.5245 StartZ=0 EndX=-2.831 EndY=-15.5245 EndZ=0
    g284: LineSegment StartX=-4.8065 StartY=-14.9613 StartZ=0 EndX=-4.8065 EndY=-12.9858 EndZ=0
    g285: LineSegment StartX=-2.831 StartY=-14.9613 StartZ=0 EndX=-2.831 EndY=-12.9858 EndZ=0
    g286: LineSegment StartX=-4.8065 StartY=-14.9613 StartZ=0 EndX=-2.831 EndY=-14.9613 EndZ=0
    g287: LineSegment StartX=-4.8065 StartY=-12.9858 StartZ=0 EndX=-2.831 EndY=-12.9858 EndZ=0
    g288: LineSegment StartX=-4.8065 StartY=-12.4226 StartZ=0 EndX=-4.8065 EndY=-10.4471 EndZ=0
    g289: LineSegment StartX=-2.831 StartY=-12.4226 StartZ=0 EndX=-2.831 EndY=-10.4471 EndZ=0
    g290: LineSegment StartX=-4.8065 StartY=-12.4226 StartZ=0 EndX=-2.831 EndY=-12.4226 EndZ=0
    g291: LineSegment StartX=-4.8065 StartY=-10.4471 StartZ=0 EndX=-2.831 EndY=-10.4471 EndZ=0
    g292: LineSegment StartX=-4.8065 StartY=-9.88385 StartZ=0 EndX=-4.8065 EndY=-7.90835 EndZ=0
    g293: LineSegment StartX=-2.831 StartY=-9.88385 StartZ=0 EndX=-2.831 EndY=-7.90835 EndZ=0
    g294: LineSegment StartX=-4.8065 StartY=-9.88385 StartZ=0 EndX=-2.831 EndY=-9.88385 EndZ=0
    g295: LineSegment StartX=-4.8065 StartY=-7.90835 StartZ=0 EndX=-2.831 EndY=-7.90835 EndZ=0
    g296: LineSegment StartX=-4.8065 StartY=-7.34515 StartZ=0 EndX=-4.8065 EndY=-5.36965 EndZ=0
    g297: LineSegment StartX=-2.831 StartY=-7.34515 StartZ=0 EndX=-2.831 EndY=-5.36965 EndZ=0
    g298: LineSegment StartX=-4.8065 StartY=-7.34515 StartZ=0 EndX=-2.831 EndY=-7.34515 EndZ=0
    g299: LineSegment StartX=-4.8065 StartY=-5.36965 StartZ=0 EndX=-2.831 EndY=-5.36965 EndZ=0
    g300: LineSegment StartX=-4.8065 StartY=-4.80645 StartZ=0 EndX=-4.8065 EndY=-2.83095 EndZ=0
    g301: LineSegment StartX=-2.831 StartY=-4.80645 StartZ=0 EndX=-2.831 EndY=-2.83095 EndZ=0
    g302: LineSegment StartX=-4.8065 StartY=-4.80645 StartZ=0 EndX=-2.831 EndY=-4.80645 EndZ=0
    g303: LineSegment StartX=-4.8065 StartY=-2.83095 StartZ=0 EndX=-2.831 EndY=-2.83095 EndZ=0
    g304: LineSegment StartX=-4.8065 StartY=-2.26775 StartZ=0 EndX=-4.8065 EndY=-0.292254 EndZ=0
    g305: LineSegment StartX=-2.831 StartY=-2.26775 StartZ=0 EndX=-2.831 EndY=-0.292254 EndZ=0
    g306: LineSegment StartX=-4.8065 StartY=-2.26775 StartZ=0 EndX=-2.831 EndY=-2.26775 EndZ=0
    g307: LineSegment StartX=-4.8065 StartY=-0.292254 StartZ=0 EndX=-2.831 EndY=-0.292254 EndZ=0
    g308: LineSegment StartX=-4.8065 StartY=0.270946 StartZ=0 EndX=-4.8065 EndY=2.24645 EndZ=0
    g309: LineSegment StartX=-2.831 StartY=0.270946 StartZ=0 EndX=-2.831 EndY=2.24645 EndZ=0
    g310: LineSegment StartX=-4.8065 StartY=0.270946 StartZ=0 EndX=-2.831 EndY=0.270946 EndZ=0
    g311: LineSegment StartX=-4.8065 StartY=2.24645 StartZ=0 EndX=-2.831 EndY=2.24645 EndZ=0
    g312: LineSegment StartX=-4.8065 StartY=2.80965 StartZ=0 EndX=-4.8065 EndY=4.78515 EndZ=0
    g313: LineSegment StartX=-2.831 StartY=2.80965 StartZ=0 EndX=-2.831 EndY=4.78515 EndZ=0
    g314: LineSegment StartX=-4.8065 StartY=2.80965 StartZ=0 EndX=-2.831 EndY=2.80965 EndZ=0
    g315: LineSegment StartX=-4.8065 StartY=4.78515 StartZ=0 EndX=-2.831 EndY=4.78515 EndZ=0
    g316: LineSegment StartX=-4.8065 StartY=5.34835 StartZ=0 EndX=-4.8065 EndY=7.32385 EndZ=0
    g317: LineSegment StartX=-2.831 StartY=5.34835 StartZ=0 EndX=-2.831 EndY=7.32385 EndZ=0
    g318: LineSegment StartX=-4.8065 StartY=5.34835 StartZ=0 EndX=-2.831 EndY=5.34835 EndZ=0
    g319: LineSegment StartX=-4.8065 StartY=7.32385 StartZ=0 EndX=-2.831 EndY=7.32385 EndZ=0
    g320: LineSegment StartX=-4.8065 StartY=7.88705 StartZ=0 EndX=-4.8065 EndY=9.86255 EndZ=0
    g321: LineSegment StartX=-2.831 StartY=7.88705 StartZ=0 EndX=-2.831 EndY=9.86255 EndZ=0
    g322: LineSegment StartX=-4.8065 StartY=7.88705 StartZ=0 EndX=-2.831 EndY=7.88705 EndZ=0
    g323: LineSegment StartX=-4.8065 StartY=9.86255 StartZ=0 EndX=-2.831 EndY=9.86255 EndZ=0
    g324: LineSegment StartX=-4.8065 StartY=10.4257 StartZ=0 EndX=-4.8065 EndY=12.4012 EndZ=0
    g325: LineSegment StartX=-2.831 StartY=10.4257 StartZ=0 EndX=-2.831 EndY=12.4012 EndZ=0
    g326: LineSegment StartX=-4.8065 StartY=10.4257 StartZ=0 EndX=-2.831 EndY=10.4257 EndZ=0
    g327: LineSegment StartX=-4.8065 StartY=12.4012 StartZ=0 EndX=-2.831 EndY=12.4012 EndZ=0
    g328: LineSegment StartX=-4.8065 StartY=12.9644 StartZ=0 EndX=-4.8065 EndY=14.9399 EndZ=0
    g329: LineSegment StartX=-2.831 StartY=12.9644 StartZ=0 EndX=-2.831 EndY=14.9399 EndZ=0
    g330: LineSegment StartX=-4.8065 StartY=12.9644 StartZ=0 EndX=-2.831 EndY=12.9644 EndZ=0
    g331: LineSegment StartX=-4.8065 StartY=14.9399 StartZ=0 EndX=-2.831 EndY=14.9399 EndZ=0
    g332: LineSegment StartX=-4.8065 StartY=15.5031 StartZ=0 EndX=-4.8065 EndY=17.4786 EndZ=0
    g333: LineSegment StartX=-2.831 StartY=15.5031 StartZ=0 EndX=-2.831 EndY=17.4786 EndZ=0
    g334: LineSegment StartX=-4.8065 StartY=15.5031 StartZ=0 EndX=-2.831 EndY=15.5031 EndZ=0
    g335: LineSegment StartX=-4.8065 StartY=17.4786 StartZ=0 EndX=-2.831 EndY=17.4786 EndZ=0
    g336: LineSegment StartX=2.8096 StartY=-17.5 StartZ=0 EndX=2.8096 EndY=-15.5245 EndZ=0
    g337: LineSegment StartX=4.7851 StartY=-17.5 StartZ=0 EndX=4.7851 EndY=-15.5245 EndZ=0
    g338: LineSegment StartX=2.8096 StartY=-17.5 StartZ=0 EndX=4.7851 EndY=-17.5 EndZ=0
    g339: LineSegment StartX=2.8096 StartY=-15.5245 StartZ=0 EndX=4.7851 EndY=-15.5245 EndZ=0
    g340: LineSegment StartX=2.8096 StartY=-14.9613 StartZ=0 EndX=2.8096 EndY=-12.9858 EndZ=0
    g341: LineSegment StartX=4.7851 StartY=-14.9613 StartZ=0 EndX=4.7851 EndY=-12.9858 EndZ=0
    g342: LineSegment StartX=2.8096 StartY=-14.9613 StartZ=0 EndX=4.7851 EndY=-14.9613 EndZ=0
    g343: LineSegment StartX=2.8096 StartY=-12.9858 StartZ=0 EndX=4.7851 EndY=-12.9858 EndZ=0
    g344: LineSegment StartX=2.8096 StartY=-12.4226 StartZ=0 EndX=2.8096 EndY=-10.4471 EndZ=0
    g345: LineSegment StartX=4.7851 StartY=-12.4226 StartZ=0 EndX=4.7851 EndY=-10.4471 EndZ=0
    g346: LineSegment StartX=2.8096 StartY=-12.4226 StartZ=0 EndX=4.7851 EndY=-12.4226 EndZ=0
    g347: LineSegment StartX=2.8096 StartY=-10.4471 StartZ=0 EndX=4.7851 EndY=-10.4471 EndZ=0
    g348: LineSegment StartX=2.8096 StartY=-9.88385 StartZ=0 EndX=2.8096 EndY=-7.90835 EndZ=0
    g349: LineSegment StartX=4.7851 StartY=-9.88385 StartZ=0 EndX=4.7851 EndY=-7.90835 EndZ=0
    g350: LineSegment StartX=2.8096 StartY=-9.88385 StartZ=0 EndX=4.7851 EndY=-9.88385 EndZ=0
    g351: LineSegment StartX=2.8096 StartY=-7.90835 StartZ=0 EndX=4.7851 EndY=-7.90835 EndZ=0
    g352: LineSegment StartX=2.8096 StartY=-7.34515 StartZ=0 EndX=2.8096 EndY=-5.36965 EndZ=0
    g353: LineSegment StartX=4.7851 StartY=-7.34515 StartZ=0 EndX=4.7851 EndY=-5.36965 EndZ=0
    g354: LineSegment StartX=2.8096 StartY=-7.34515 StartZ=0 EndX=4.7851 EndY=-7.34515 EndZ=0
    g355: LineSegment StartX=2.8096 StartY=-5.36965 StartZ=0 EndX=4.7851 EndY=-5.36965 EndZ=0
    g356: LineSegment StartX=2.8096 StartY=-4.80645 StartZ=0 EndX=2.8096 EndY=-2.83095 EndZ=0
    g357: LineSegment StartX=4.7851 StartY=-4.80645 StartZ=0 EndX=4.7851 EndY=-2.83095 EndZ=0
    g358: LineSegment StartX=2.8096 StartY=-4.80645 StartZ=0 EndX=4.7851 EndY=-4.80645 EndZ=0
    g359: LineSegment StartX=2.8096 StartY=-2.83095 StartZ=0 EndX=4.7851 EndY=-2.83095 EndZ=0
    g360: LineSegment StartX=2.8096 StartY=-2.26775 StartZ=0 EndX=2.8096 EndY=-0.292254 EndZ=0
    g361: LineSegment StartX=4.7851 StartY=-2.26775 StartZ=0 EndX=4.7851 EndY=-0.292254 EndZ=0
    g362: LineSegment StartX=2.8096 StartY=-2.26775 StartZ=0 EndX=4.7851 EndY=-2.26775 EndZ=0
    g363: LineSegment StartX=2.8096 StartY=-0.292254 StartZ=0 EndX=4.7851 EndY=-0.292254 EndZ=0
    g364: LineSegment StartX=2.8096 StartY=0.270946 StartZ=0 EndX=2.8096 EndY=2.24645 EndZ=0
    g365: LineSegment StartX=4.7851 StartY=0.270946 StartZ=0 EndX=4.7851 EndY=2.24645 EndZ=0
    g366: LineSegment StartX=2.8096 StartY=0.270946 StartZ=0 EndX=4.7851 EndY=0.270946 EndZ=0
    g367: LineSegment StartX=2.8096 StartY=2.24645 StartZ=0 EndX=4.7851 EndY=2.24645 EndZ=0
    g368: LineSegment StartX=2.8096 StartY=2.80965 StartZ=0 EndX=2.8096 EndY=4.78515 EndZ=0
    g369: LineSegment StartX=4.7851 StartY=2.80965 StartZ=0 EndX=4.7851 EndY=4.78515 EndZ=0
    g370: LineSegment StartX=2.8096 StartY=2.80965 StartZ=0 EndX=4.7851 EndY=2.80965 EndZ=0
    g371: LineSegment StartX=2.8096 StartY=4.78515 StartZ=0 EndX=4.7851 EndY=4.78515 EndZ=0
    g372: LineSegment StartX=2.8096 StartY=5.34835 StartZ=0 EndX=2.8096 EndY=7.32385 EndZ=0
    g373: LineSegment StartX=4.7851 StartY=5.34835 StartZ=0 EndX=4.7851 EndY=7.32385 EndZ=0
    g374: LineSegment StartX=2.8096 StartY=5.34835 StartZ=0 EndX=4.7851 EndY=5.34835 EndZ=0
    g375: LineSegment StartX=2.8096 StartY=7.32385 StartZ=0 EndX=4.7851 EndY=7.32385 EndZ=0
    g376: LineSegment StartX=2.8096 StartY=7.88705 StartZ=0 EndX=2.8096 EndY=9.86255 EndZ=0
    g377: LineSegment StartX=4.7851 StartY=7.88705 StartZ=0 EndX=4.7851 EndY=9.86255 EndZ=0
    g378: LineSegment StartX=2.8096 StartY=7.88705 StartZ=0 EndX=4.7851 EndY=7.88705 EndZ=0
    g379: LineSegment StartX=2.8096 StartY=9.86255 StartZ=0 EndX=4.7851 EndY=9.86255 EndZ=0
    g380: LineSegment StartX=2.8096 StartY=10.4257 StartZ=0 EndX=2.8096 EndY=12.4012 EndZ=0
    g381: LineSegment StartX=4.7851 StartY=10.4257 StartZ=0 EndX=4.7851 EndY=12.4012 EndZ=0
    g382: LineSegment StartX=2.8096 StartY=10.4257 StartZ=0 EndX=4.7851 EndY=10.4257 EndZ=0
    g383: LineSegment StartX=2.8096 StartY=12.4012 StartZ=0 EndX=4.7851 EndY=12.4012 EndZ=0
    g384: LineSegment StartX=2.8096 StartY=12.9644 StartZ=0 EndX=2.8096 EndY=14.9399 EndZ=0
    g385: LineSegment StartX=4.7851 StartY=12.9644 StartZ=0 EndX=4.7851 EndY=14.9399 EndZ=0
    g386: LineSegment StartX=2.8096 StartY=12.9644 StartZ=0 EndX=4.7851 EndY=12.9644 EndZ=0
    g387: LineSegment StartX=2.8096 StartY=14.9399 StartZ=0 EndX=4.7851 EndY=14.9399 EndZ=0
    g388: LineSegment StartX=2.8096 StartY=15.5031 StartZ=0 EndX=2.8096 EndY=17.4786 EndZ=0
    g389: LineSegment StartX=4.7851 StartY=15.5031 StartZ=0 EndX=4.7851 EndY=17.4786 EndZ=0
    g390: LineSegment StartX=2.8096 StartY=15.5031 StartZ=0 EndX=4.7851 EndY=15.5031 EndZ=0
    g391: LineSegment StartX=2.8096 StartY=17.4786 StartZ=0 EndX=4.7851 EndY=17.4786 EndZ=0
    g392: LineSegment StartX=5.3483 StartY=-17.5 StartZ=0 EndX=5.3483 EndY=-15.5245 EndZ=0
    g393: LineSegment StartX=7.3238 StartY=-17.5 StartZ=0 EndX=7.3238 EndY=-15.5245 EndZ=0
    g394: LineSegment StartX=5.3483 StartY=-17.5 StartZ=0 EndX=7.3238 EndY=-17.5 EndZ=0
    g395: LineSegment StartX=5.3483 StartY=-15.5245 StartZ=0 EndX=7.3238 EndY=-15.5245 EndZ=0
    g396: LineSegment StartX=5.3483 StartY=-14.9613 StartZ=0 EndX=5.3483 EndY=-12.9858 EndZ=0
    g397: LineSegment StartX=7.3238 StartY=-14.9613 StartZ=0 EndX=7.3238 EndY=-12.9858 EndZ=0
    g398: LineSegment StartX=5.3483 StartY=-14.9613 StartZ=0 EndX=7.3238 EndY=-14.9613 EndZ=0
    g399: LineSegment StartX=5.3483 StartY=-12.9858 StartZ=0 EndX=7.3238 EndY=-12.9858 EndZ=0
    ... +272 more geometry lines
FEATURE [PartDesign::Pad] Pad
  BaseFeature = -> Box
  Direction = (0,0,1)
  Length = 18
  Length2 = 10
  Placement = pos=(-17.5,-17.5,0) rot=(0,0,1;0rad)
  Profile = -> Sketch001
  ReferenceAxis = -> Sketch001 [N_Axis]
  Type = 0
FEATURE [PartDesign::Fillet] Fillet008
  Base = -> Pad [Edge116,Edge124,Edge132,Edge140,Edge184,Edge192,Edge200,Edge412,Edge420,Edge428,Edge484,Edge492,Edge500,Edge508,Edge206,Edge210,Edge230,Edge234,Edge302,Edge314,Edge318,Edge514,Edge518,Edge538,Edge586,Edge590,Edge610,Edge614]
  BaseFeature = -> Pad
  Placement = pos=(-17.5,-17.5,0) rot=(0,0,1;0rad)
  Radius = 2.82
  SupportTransform = false
  UseAllEdges = false
FEATURE [PartDesign::Body] Body  label="Main"
  Group = -> [Box,Sketch001,Pad,Fillet008]
  Origin = -> Origin
  Placement = pos=(0,0,0.05) rot=(0,0,1;1.5708rad)
  Tip = -> Fillet008
FEATURE [PartDesign::Chamfer] Chamfer
  Angle = 50
  Base = -> Box013 [Edge23,Edge39]
  BaseFeature = -> Box013
  ChamferType = 2
  FlipDirection = false
  Placement = pos=(22.5,-15,2.5) rot=(0,0,1;0rad)
  Size = 0.499
  Size2 = 1
  SupportTransform = false
  UseAllEdges = false
FEATURE [PartDesign::Chamfer] Chamfer001
  Angle = 40
  Base = -> Chamfer [Edge85,Edge26]
  BaseFeature = -> Chamfer
  ChamferType = 2
  FlipDirection = false
  Placement = pos=(22.5,-15,2.5) rot=(0,0,1;0rad)
  Size = 0.5955
  Size2 = 1
  SupportTransform = false
  UseAllEdges = false
FEATURE [PartDesign::Body] Body001  label="spring-arms"
  Group = -> [Box010,Box011,Box012,Fillet,Fillet001,Fillet002,Box013,Chamfer,Chamfer001]
  Origin = -> Origin001
  Placement = pos=(0,-0.55,0) rot=(0,0,1;0rad)
  Tip = -> Chamfer001
FEATURE [App::Part] Part  label="Aavid_374724B60024G"
  Group = -> [Body002,Body001,Body,Body003,Shape2DView,Array]
  Origin = -> Origin003
